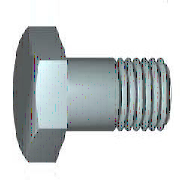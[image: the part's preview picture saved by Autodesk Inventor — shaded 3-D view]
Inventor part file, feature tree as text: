
AUTODESK INVENTOR PART (.ipt)
format: ipt  version: 2024.2 (Build 282272000, 272)  size: 204,800 bytes
history: native  units: mm
features: sketch x2, projected_geometry x1
ambient origin geometry x8: Origin, YZ Plane, XZ Plane, XY Plane, X Axis, Y Axis, Z Axis, Center Point
bodies: Solid1 (feature_tree)
feature tree (3):
  sketch  "草图4"  dims[d22=60.0deg]
  sketch  "草图6"  dims[d25=90.0deg d27=21.0mm d28=6.7mm d29=0.0mm d30=4.363323mm d31=21.0mm d32=90.0deg d33=30.0mm d34=0.0mm d35=1.073538mm d36=2.0mm d37=45.0deg d39=0.0mm d40=0.0mm d41=0.0mm]
  projected_geometry  "投影回路2"
